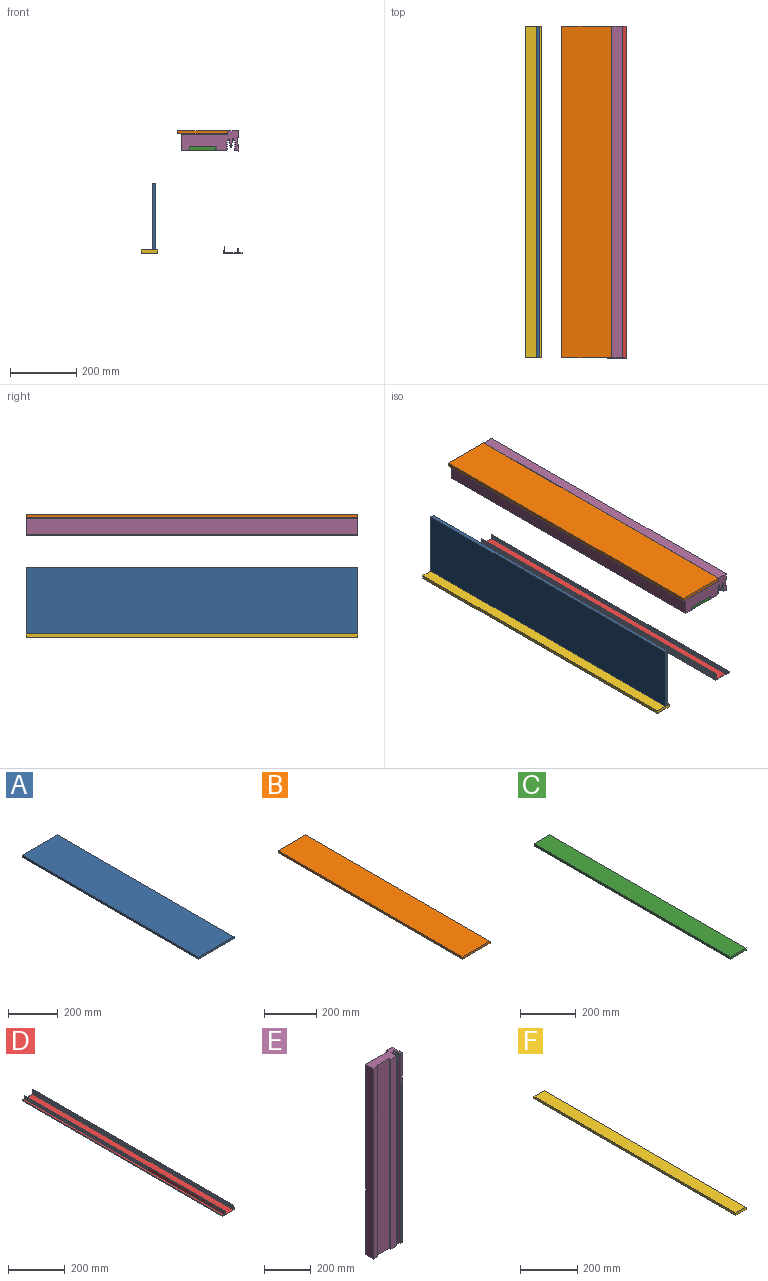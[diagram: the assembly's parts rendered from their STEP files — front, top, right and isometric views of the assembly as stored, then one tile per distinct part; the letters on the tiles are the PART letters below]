
ASSEMBLY  parts=6 mates=1
PART A: 6 faces, bbox 200x1000x10 mm
  f0: plane 1000x10mm, normal (-1,0,0), area 10000mm2, adj f1,f3,f4,f5
  f1: plane 1000x200mm, normal (0,0,-1), area 200000mm2, adj f0,f2,f4,f5
  f2: plane 1000x10mm, normal (1,0,0), area 10000mm2, adj f1,f3,f4,f5
  f3: plane 1000x200mm, normal (0,0,1), area 200000mm2, adj f0,f2,f4,f5
  f4: plane 200x10mm, normal (0,-1,0), area 2000mm2, adj f0,f1,f2,f3
  f5: plane 200x10mm, normal (0,1,0), area 2000mm2, adj f0,f1,f2,f3
PART B: 6 faces, bbox 150x1000x10 mm
  f0: plane 1000x10mm, normal (-1,0,0), area 10000mm2, adj f1,f3,f4,f5
  f1: plane 1000x150mm, normal (0,0,-1), area 150000mm2, adj f0,f2,f4,f5
  f2: plane 1000x10mm, normal (1,0,0), area 10000mm2, adj f1,f3,f4,f5
  f3: plane 1000x150mm, normal (0,0,1), area 150000mm2, adj f0,f2,f4,f5
  f4: plane 150x10mm, normal (0,-1,0), area 1500mm2, adj f0,f1,f2,f3
  f5: plane 150x10mm, normal (0,1,0), area 1500mm2, adj f0,f1,f2,f3
PART C: 6 faces, bbox 80x1000x10 mm
  f0: plane 1000x10mm, normal (-1,0,0), area 10000mm2, adj f1,f3,f4,f5
  f1: plane 1000x80mm, normal (0,0,-1), area 80000mm2, adj f0,f2,f4,f5
  f2: plane 1000x10mm, normal (1,0,0), area 10000mm2, adj f1,f3,f4,f5
  f3: plane 1000x80mm, normal (0,0,1), area 80000mm2, adj f0,f2,f4,f5
  f4: plane 80x10mm, normal (0,-1,0), area 800mm2, adj f0,f1,f2,f3
  f5: plane 80x10mm, normal (0,1,0), area 800mm2, adj f0,f1,f2,f3
PART D: 62 faces, bbox 57.5x1000x21 mm
  f0: plane 1000x14.3mm, normal (-1,0,0), area 14303.9mm2, adj f1,f2,f60,f61
  f1: plane 57.5x21mm, normal (0,-1,0), area 145.8mm2, adj f0,f2,f3,f4,f5,f6,f7,f8
  f2: plane 1000x11mm, normal (0,0,1), area 11000mm2, adj f0,f1,f3,f60
  f3: plane 1000x1.5mm, normal (1,0,0), area 1500mm2, adj f1,f2,f4,f60
  f4: plane 1000x1.5mm, normal (0,0,1), area 1500mm2, adj f1,f3,f5,f60
  f5: plane 1000x3mm, normal (-1,0,0), area 3000mm2, adj f1,f4,f6,f60
  f6: plane 1000x57.5mm, normal (0,0,-1), area 57500mm2, adj f1,f5,f7,f60
  f7: plane 1000x4mm, normal (1,0,0), area 4000mm2, adj f1,f6,f8,f60
  f8: plane 1000x1mm, normal (0,0,1), area 1000mm2, adj f1,f7,f9,f60
  f9: plane 1000x3mm, normal (-1,0,0), area 3000mm2, adj f1,f8,f10,f60
  f10: plane 1000x1mm, normal (0,0,1), area 1000mm2, adj f1,f9,f11,f60
  f11: plane 1000x7mm, normal (1,0,0), area 7000mm2, adj f1,f10,f12,f60
  f12: plane 1000x1mm, normal (0,0,-1), area 1000mm2, adj f1,f11,f13,f60
  f13: plane 1000x3mm, normal (-1,0,0), area 3000mm2, adj f1,f12,f14,f60
  f14: plane 1000x1mm, normal (0,0,-1), area 1000mm2, adj f1,f13,f15,f60
  f15: plane 1000x4mm, normal (1,0,0), area 4000mm2, adj f1,f14,f16,f60
  f16: plane 1000x2mm, normal (0,0,1), area 2000mm2, adj f1,f15,f17,f60
  f17: plane 1000x12mm, normal (1,0,0), area 12000mm2, adj f1,f16,f18,f60
  f18: plane 1000x1mm, normal (0,0,1), area 1000mm2, adj f1,f17,f19,f60
  f19: plane 1000x1.73mm, normal (-0.87,0,0.5), area 2000mm2, adj f1,f18,f20,f60
  f20: plane 1000x1mm, normal (0,0,-1), area 1000mm2, adj f1,f19,f21,f60
  f21: plane 1000x1.73mm, normal (-0.87,0,0.5), area 2000mm2, adj f1,f20,f22,f60
  f22: plane 1000x1mm, normal (0,0,-1), area 1000mm2, adj f1,f21,f23,f60
  f23: plane 1000x1.73mm, normal (-0.87,0,0.5), area 2000mm2, adj f1,f22,f24,f60
  f24: plane 1000x1mm, normal (0,0,-1), area 1000mm2, adj f1,f23,f25,f60
  f25: plane 1000x1.73mm, normal (-0.87,0,0.5), area 2000mm2, adj f1,f24,f26,f60
  f26: plane 1000x1mm, normal (0,0,-1), area 1000mm2, adj f1,f25,f27,f60
  f27: plane 1000x1.73mm, normal (-0.87,0,0.5), area 2000mm2, adj f1,f26,f28,f60
  f28: plane 1000x1mm, normal (0,0,-1), area 1000mm2, adj f1,f27,f29,f60
  f29: plane 1000x1.73mm, normal (-0.87,0,0.5), area 2000mm2, adj f1,f28,f30,f60
  f30: plane 1000x1mm, normal (0,0,-1), area 1000mm2, adj f1,f29,f31,f60
  f31: plane 1000x1.73mm, normal (-0.87,0,0.5), area 2000mm2, adj f1,f30,f32,f60
  f32: plane 1000x1mm, normal (0,0,-1), area 1000mm2, adj f1,f31,f33,f60
  f33: plane 1000x1.73mm, normal (-0.87,0,0.5), area 2000mm2, adj f1,f32,f34,f60
  f34: plane 1000x1mm, normal (0,0,-1), area 1000mm2, adj f1,f33,f35,f60
  f35: plane 1000x1.73mm, normal (-0.87,0,0.5), area 2000mm2, adj f1,f34,f36,f60
  f36: plane 1000x1mm, normal (0,0,-1), area 1000mm2, adj f1,f35,f37,f60
  f37: plane 1000x1.73mm, normal (-0.87,0,0.5), area 2000mm2, adj f1,f36,f38,f60
  f38: plane 1000x1mm, normal (0,0,-1), area 1000mm2, adj f1,f37,f39,f60
  f39: plane 1000x1.73mm, normal (-0.87,0,0.5), area 2000mm2, adj f1,f38,f40,f60
  f40: plane 1000x1mm, normal (0,0,-1), area 1000mm2, adj f1,f39,f41,f60
  f41: plane 1000x0.45mm, normal (-1,0,0), area 447.4mm2, adj f1,f40,f42,f60
  f42: plane 1000x41mm, normal (0,0,1), area 41000mm2, adj f1,f41,f43,f60
  f43: plane 1000x0.45mm, normal (1,0,0), area 447.4mm2, adj f1,f42,f44,f60
  f44: plane 1000x1mm, normal (0,0,-1), area 1000mm2, adj f1,f43,f45,f60
  f45: plane 1000x1.73mm, normal (0.87,0,0.5), area 2000mm2, adj f1,f44,f46,f60
  f46: plane 1000x1mm, normal (0,0,-1), area 1000mm2, adj f1,f45,f47,f60
  f47: plane 1000x1.73mm, normal (0.87,0,0.5), area 2000mm2, adj f1,f46,f48,f60
  f48: plane 1000x1mm, normal (0,0,-1), area 1000mm2, adj f1,f47,f49,f60
  f49: plane 1000x1.73mm, normal (0.87,0,0.5), area 2000mm2, adj f1,f48,f50,f60
  f50: plane 1000x1mm, normal (0,0,-1), area 1000mm2, adj f1,f49,f51,f60
  f51: plane 1000x1.73mm, normal (0.87,0,0.5), area 2000mm2, adj f1,f50,f52,f60
  f52: plane 1000x1mm, normal (0,0,-1), area 1000mm2, adj f1,f51,f53,f60
  f53: plane 1000x1.73mm, normal (0.87,0,0.5), area 2000mm2, adj f1,f52,f54,f60
  f54: plane 1000x1mm, normal (0,0,-1), area 1000mm2, adj f1,f53,f55,f60
  f55: plane 1000x1.73mm, normal (0.87,0,0.5), area 2000mm2, adj f1,f54,f56,f60
  f56: plane 1000x1mm, normal (0,0,-1), area 1000mm2, adj f1,f55,f57,f60
  f57: plane 1000x1.73mm, normal (0.87,0,0.5), area 2000mm2, adj f1,f56,f58,f60
  f58: plane 1000x1mm, normal (0,0,-1), area 1000mm2, adj f1,f57,f59,f60
  f59: plane 1000x1.73mm, normal (0.87,0,0.5), area 2000mm2, adj f1,f58,f60,f61
  f60: plane 57.5x21mm, normal (0,1,0), area 145.8mm2, adj f0,f2,f3,f4,f5,f6,f7,f8
  f61: plane 1000x1mm, normal (0,0,1), area 1000mm2, adj f0,f1,f59,f60
PART E: 55 faces, bbox 173x62x1000 mm
  f0: plane 1000x140.25mm, normal (0,1,0), area 140250mm2, adj f1,f2,f42,f54
  f1: plane 173x62.05mm, normal (0,0,1), area 7464.2mm2, adj f0,f3,f4,f5,f6,f7,f8,f9
  f2: plane 173x62.05mm, normal (0,0,-1), area 7464.2mm2, adj f0,f3,f4,f5,f6,f7,f8,f9
  f3: plane 1000x22mm, normal (1,0,0), area 22000mm2, adj f1,f2,f41,f51
  f4: plane 1000x5.98mm, normal (0.89,-0.45,0), area 6689.2mm2, adj f1,f2,f5,f49
  f5: plane 1000x2.99mm, normal (-0.03,1,0), area 2994.3mm2, adj f1,f2,f4,f6
  f6: plane 1000x5.98mm, normal (0.89,-0.45,0), area 6689.2mm2, adj f1,f2,f5,f7
  f7: plane 1000x2.99mm, normal (-0.03,1,0), area 2994.3mm2, adj f1,f2,f6,f8
  f8: plane 1000x5.98mm, normal (0.89,-0.45,0), area 6689.2mm2, adj f1,f2,f7,f9
  f9: plane 1000x2.99mm, normal (-0.03,1,0), area 2994.3mm2, adj f1,f2,f8,f10
  f10: plane 1000x5mm, normal (0.89,-0.45,0), area 5590.2mm2, adj f1,f2,f9,f11
  f11: cylinder r=9.8mm len=1000mm, axis (0,0,-1), area 6307.9mm2, adj f1,f2,f10,f12
  f12: cylinder r=0.5mm len=1000mm, axis (0,0,-1), area 956.1mm2, adj f1,f2,f11,f13
  f13: plane 1000x4.57mm, normal (-0.99,-0.15,0), area 4614.4mm2, adj f1,f2,f12,f14
  f14: plane 1000x1.5mm, normal (0.25,0.97,0), area 1552mm2, adj f1,f2,f13,f15
  f15: plane 1000x2.65mm, normal (-0.79,-0.62,0), area 3377.8mm2, adj f1,f2,f14,f16
  f16: plane 1000x13.5mm, normal (-0.98,-0.19,0), area 13744.8mm2, adj f1,f2,f15,f17
  f17: plane 1000x1.67mm, normal (0.25,0.97,0), area 1726.5mm2, adj f1,f2,f16,f18
  f18: plane 1000x2.65mm, normal (-0.79,-0.62,0), area 3377.8mm2, adj f1,f2,f17,f19
  f19: plane 1000x2.67mm, normal (-0.98,-0.19,0), area 2722.2mm2, adj f1,f2,f18,f20
  f20: cylinder r=1mm len=1000mm, axis (0,0,-1), area 2628mm2, adj f1,f2,f19,f21
  f21: plane 1000x2.67mm, normal (0.98,-0.19,0), area 2722.2mm2, adj f1,f2,f20,f22
  f22: plane 1000x2.65mm, normal (0.79,-0.62,0), area 3377.8mm2, adj f1,f2,f21,f23
  f23: plane 1000x1.67mm, normal (-0.25,0.97,0), area 1726.5mm2, adj f1,f2,f22,f24
  f24: plane 1000x13.5mm, normal (0.98,-0.19,0), area 13744.8mm2, adj f1,f2,f23,f25
  f25: plane 1000x2.65mm, normal (0.79,-0.62,0), area 3377.8mm2, adj f1,f2,f24,f26
  f26: plane 1000x1.5mm, normal (-0.25,0.97,0), area 1552mm2, adj f1,f2,f25,f27
  f27: plane 1000x4.57mm, normal (0.99,-0.15,0), area 4614.4mm2, adj f1,f2,f26,f28
  f28: cylinder r=0.5mm len=1000mm, axis (0,0,-1), area 956.1mm2, adj f1,f2,f27,f29
  f29: cylinder r=9.8mm len=1000mm, axis (0,0,-1), area 6307.9mm2, adj f1,f2,f28,f30
  f30: plane 1000x4.99mm, normal (-0.89,-0.45,0), area 5579.7mm2, adj f1,f2,f29,f31
  f31: plane 1000x2.99mm, normal (0.02,1,0), area 2994.2mm2, adj f1,f2,f30,f32
  f32: plane 1000x5.97mm, normal (-0.89,-0.45,0), area 6678.8mm2, adj f1,f2,f31,f33
  f33: plane 1000x2.99mm, normal (0.02,1,0), area 2994.2mm2, adj f1,f2,f32,f34
  f34: plane 1000x5.97mm, normal (-0.89,-0.45,0), area 6678.8mm2, adj f1,f2,f33,f35
  f35: plane 1000x2.99mm, normal (0.02,1,0), area 2994.2mm2, adj f1,f2,f34,f36
  f36: plane 1000x5.97mm, normal (-0.89,-0.45,0), area 6678.8mm2, adj f1,f2,f35,f37
  f37: plane 1000x2.99mm, normal (0.02,1,0), area 2994.2mm2, adj f1,f2,f36,f38
  f38: plane 1000x6.88mm, normal (-0.94,-0.35,0), area 7354.5mm2, adj f1,f2,f37,f39
  f39: plane 1000x9.06mm, normal (0,-1,0), area 9060.8mm2, adj f1,f2,f38,f53
  f40: plane 1000x20.05mm, normal (1,0,0), area 20047.3mm2, adj f1,f2,f50,f53
  f41: plane 1000x32.75mm, normal (0,1,0), area 32750mm2, adj f1,f2,f3,f42
  f42: plane 1000x10.5mm, normal (-1,0,0), area 10500mm2, adj f0,f1,f2,f41
  f43: plane 1000x24.75mm, normal (0,-1,0), area 24750mm2, adj f1,f2,f44,f54
  f44: plane 1000x10.5mm, normal (1,0,0), area 10500mm2, adj f1,f2,f43,f45
  f45: plane 1000x80.5mm, normal (0,-1,0), area 80500mm2, adj f1,f2,f44,f46
  f46: plane 1000x10.5mm, normal (-1,0,0), area 10500mm2, adj f1,f2,f45,f47
  f47: plane 1000x32.75mm, normal (0,-1,0), area 32750mm2, adj f1,f2,f46,f48
  f48: plane 1000x6.88mm, normal (0.94,-0.35,0), area 7354.5mm2, adj f1,f2,f47,f49
  f49: plane 1000x2.99mm, normal (-0.03,1,0), area 2994.3mm2, adj f1,f2,f4,f48
  f50: plane 1000x2mm, normal (-0.71,0.71,0), area 2828.4mm2, adj f1,f2,f40,f52
  f51: plane 1000x2mm, normal (-0.71,-0.71,0), area 2828.4mm2, adj f1,f2,f3,f52
  f52: plane 1000x24mm, normal (1,0,0), area 24000mm2, adj f1,f2,f50,f51
  f53: plane 1000x2.05mm, normal (-0.76,-0.65,0), area 2686.3mm2, adj f1,f2,f39,f40
  f54: plane 1000x49.5mm, normal (-1,0,0), area 49500mm2, adj f0,f1,f2,f43
PART F: 6 faces, bbox 50x1000x10 mm
  f0: plane 1000x10mm, normal (-1,0,0), area 10000mm2, adj f1,f3,f4,f5
  f1: plane 1000x50mm, normal (0,0,-1), area 50000mm2, adj f0,f2,f4,f5
  f2: plane 1000x10mm, normal (1,0,0), area 10000mm2, adj f1,f3,f4,f5
  f3: plane 1000x50mm, normal (0,0,1), area 50000mm2, adj f0,f2,f4,f5
  f4: plane 50x10mm, normal (0,-1,0), area 500mm2, adj f0,f1,f2,f3
  f5: plane 50x10mm, normal (0,1,0), area 500mm2, adj f0,f1,f2,f3
PLACE A rot(axis=(0,1,0),90deg) t=(-266.58,500,-94.72)mm
PLACE B t=(-190.83,500,55.28)mm fixed
PLACE C t=(-155.83,500,5.78)mm
PLACE D rot(axis=(0,0,1),180deg) t=(-52.58,-500,-305.22)mm
PLACE E rot(axis=(1,0,0),90deg) t=(-173.78,500,-111.06)mm
PLACE F t=(-300.58,500,-304.72)mm
MATE fastened C.f4 <-> E.f1  axis (0,-1,0) through (-155.83,-500,15.78)mm
